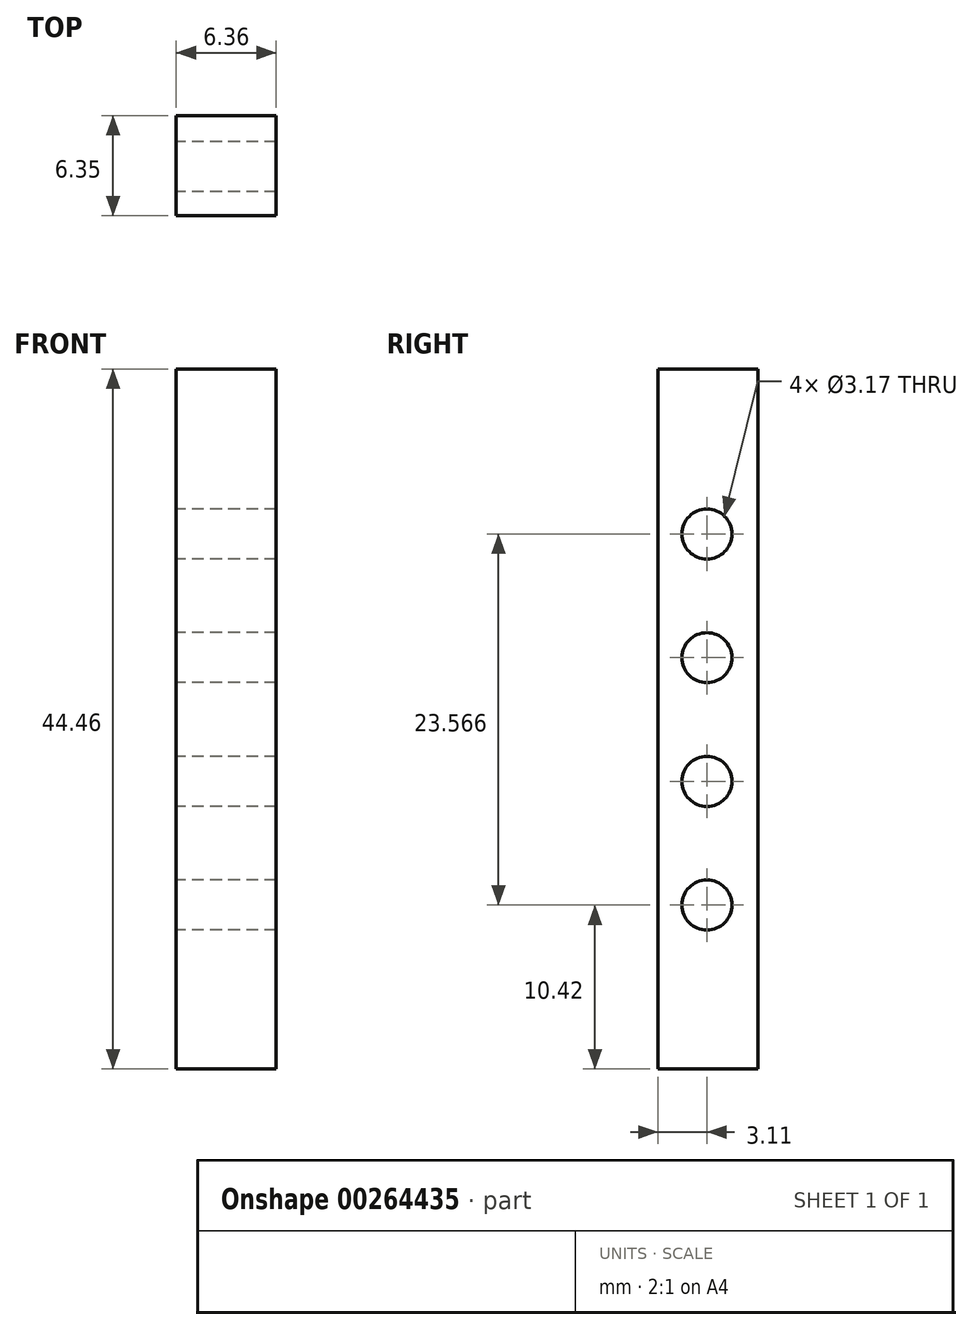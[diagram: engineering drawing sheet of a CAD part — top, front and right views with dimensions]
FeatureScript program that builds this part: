
annotation { "Feature Type Name" : "Feature", "Feature Type Description" : "" }
export const myFeature = defineFeature(function(context is Context, id is Id, definition is map)
    precondition{}
    {
        {
            var Q0;
            Q0=qCreatedBy(makeId("Front.planeOp"),FACE);
            var sketch = newSketch(context, id + "F0", { "sketchPlane" : qUnion([Q0])});
            skLineSegment(sketch, "E0.bottom", {"start": v(3.17, 22.22) * mm, "end": v(-3.18, 22.22) * mm});
            skLineSegment(sketch, "E0.top", {"start": v(3.17, -22.23) * mm, "end": v(-3.18, -22.23) * mm});
            skLineSegment(sketch, "E0.left", {"start": v(3.17, 22.22) * mm, "end": v(3.17, -22.23) * mm});
            skLineSegment(sketch, "E0.right", {"start": v(-3.18, 22.22) * mm, "end": v(-3.18, -22.23) * mm});
            skPoint(sketch, "E0.middle", {"position": v(0, 0) * mm});
            skSolve(sketch);
        }
        {
            var Q0;
            Q0 = qSketchRegion(id + "F0", true);
            extrude(context, id + "F1", {"entities" : qUnion([Q0]), "depth" : 6.35 * mm, "offsetDistance" : 25.4 * mm});
        }
        {
            var Q0;
            Q0=makeQuery(id+"F1.opExtrude","SWEPT_FACE",FACE,{"disambiguationData":[OSD([sQuery(id+"F0.wireOp",EDGE,"E0.right")])]});
            var sketch = newSketch(context, id + "F2", { "sketchPlane" : qUnion([Q0])});
            skCircle(sketch, "E1", {"center": v(3.24, 11.76) * mm, "radius": 1.59 * mm});
            skCircle(sketch, "E2", {"center": v(3.24, 3.9) * mm, "radius": 1.59 * mm});
            skPoint(sketch, "E2.centerSnap0", {"position": v(6.22, 3.9) * mm});
            skCircle(sketch, "E3", {"center": v(3.24, -3.95) * mm, "radius": 1.59 * mm});
            skCircle(sketch, "E4", {"center": v(3.24, -11.8) * mm, "radius": 1.59 * mm});
            skSolve(sketch);
        }
        {
            var Q0;
            Q0 = qSketchRegion(id + "F2", true);
            extrude(context, id + "F3", {"entities" : qUnion([Q0]), "operationType" : NewBodyOperationType.REMOVE, "oppositeDirection" : true, "depth" : 6.35 * mm, "offsetDistance" : 25.4 * mm});
        }
    });
